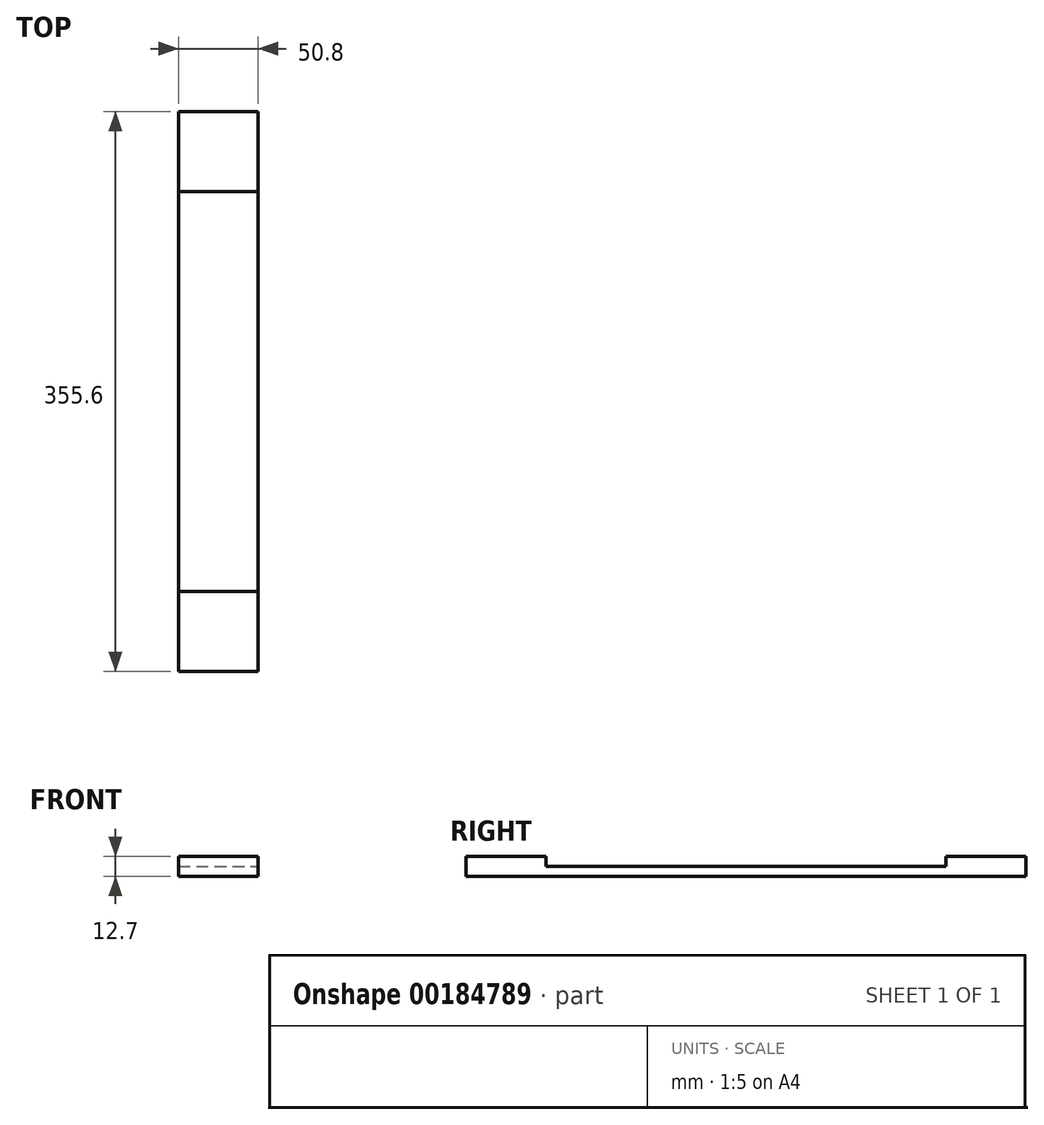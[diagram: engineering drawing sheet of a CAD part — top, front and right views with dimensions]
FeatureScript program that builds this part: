
annotation { "Feature Type Name" : "Feature", "Feature Type Description" : "" }
export const myFeature = defineFeature(function(context is Context, id is Id, definition is map)
    precondition{}
    {
        {
            var Q0;
            Q0=qCreatedBy(makeId("Top.planeOp"),FACE);
            var sketch = newSketch(context, id + "F0", { "sketchPlane" : qUnion([Q0])});
            skLineSegment(sketch, "E0.bottom", {"start": v(25.4, 177.8) * mm, "end": v(-25.4, 177.8) * mm});
            skLineSegment(sketch, "E0.top", {"start": v(25.4, -177.8) * mm, "end": v(-25.4, -177.8) * mm});
            skLineSegment(sketch, "E0.left", {"start": v(25.4, 177.8) * mm, "end": v(25.4, -177.8) * mm});
            skLineSegment(sketch, "E0.right", {"start": v(-25.4, 177.8) * mm, "end": v(-25.4, -177.8) * mm});
            skPoint(sketch, "E0.middle", {"position": v(0, 0) * mm});
            skSolve(sketch);
        }
        {
            var Q0;
            Q0=makeQuery(id+"F0.imprint","IMPRINT",FACE,{"disambiguationData":[TD([[makeQuery(id+"F0.imprint","IMPRINT",EDGE,{"derivedFrom":sQuery(id+"F0.wireOp",EDGE,"E0.bottom")}),1.0]])]});
            extrude(context, id + "F1", {"entities" : qUnion([Q0]), "depth" : 6.35 * mm});
        }
        {
            var Q0;
            Q0=makeQuery(id+"F1.opExtrude","CAP_FACE",FACE,{"disambiguationData":[OSD([sQuery(id+"F0.wireOp",EDGE,"E0.bottom"),sQuery(id+"F0.wireOp",EDGE,"E0.top"),sQuery(id+"F0.wireOp",EDGE,"E0.left"),sQuery(id+"F0.wireOp",EDGE,"E0.right")])],"isStart":false});
            var sketch = newSketch(context, id + "F2", { "sketchPlane" : qUnion([Q0])});
            skLineSegment(sketch, "E1.bottom", {"start": v(-25.4, -177.8) * mm, "end": v(25.4, -177.8) * mm});
            skLineSegment(sketch, "E1.top", {"start": v(-25.4, -127) * mm, "end": v(25.4, -127) * mm});
            skLineSegment(sketch, "E1.left", {"start": v(-25.4, -177.8) * mm, "end": v(-25.4, -127) * mm});
            skLineSegment(sketch, "E1.right", {"start": v(25.4, -177.8) * mm, "end": v(25.4, -127) * mm});
            skLineSegment(sketch, "E2.bottom", {"start": v(-25.4, 177.8) * mm, "end": v(25.4, 177.8) * mm});
            skLineSegment(sketch, "E2.top", {"start": v(-25.4, 127) * mm, "end": v(25.4, 127) * mm});
            skLineSegment(sketch, "E2.left", {"start": v(-25.4, 177.8) * mm, "end": v(-25.4, 127) * mm});
            skLineSegment(sketch, "E2.right", {"start": v(25.4, 177.8) * mm, "end": v(25.4, 127) * mm});
            skSolve(sketch);
        }
        {
            var Q0;
            Q0=qSketchRegion(id+"F2",true);
            extrude(context, id + "F3", {"entities" : qUnion([Q0]), "operationType" : NewBodyOperationType.ADD, "depth" : 6.35 * mm});
        }
    });
